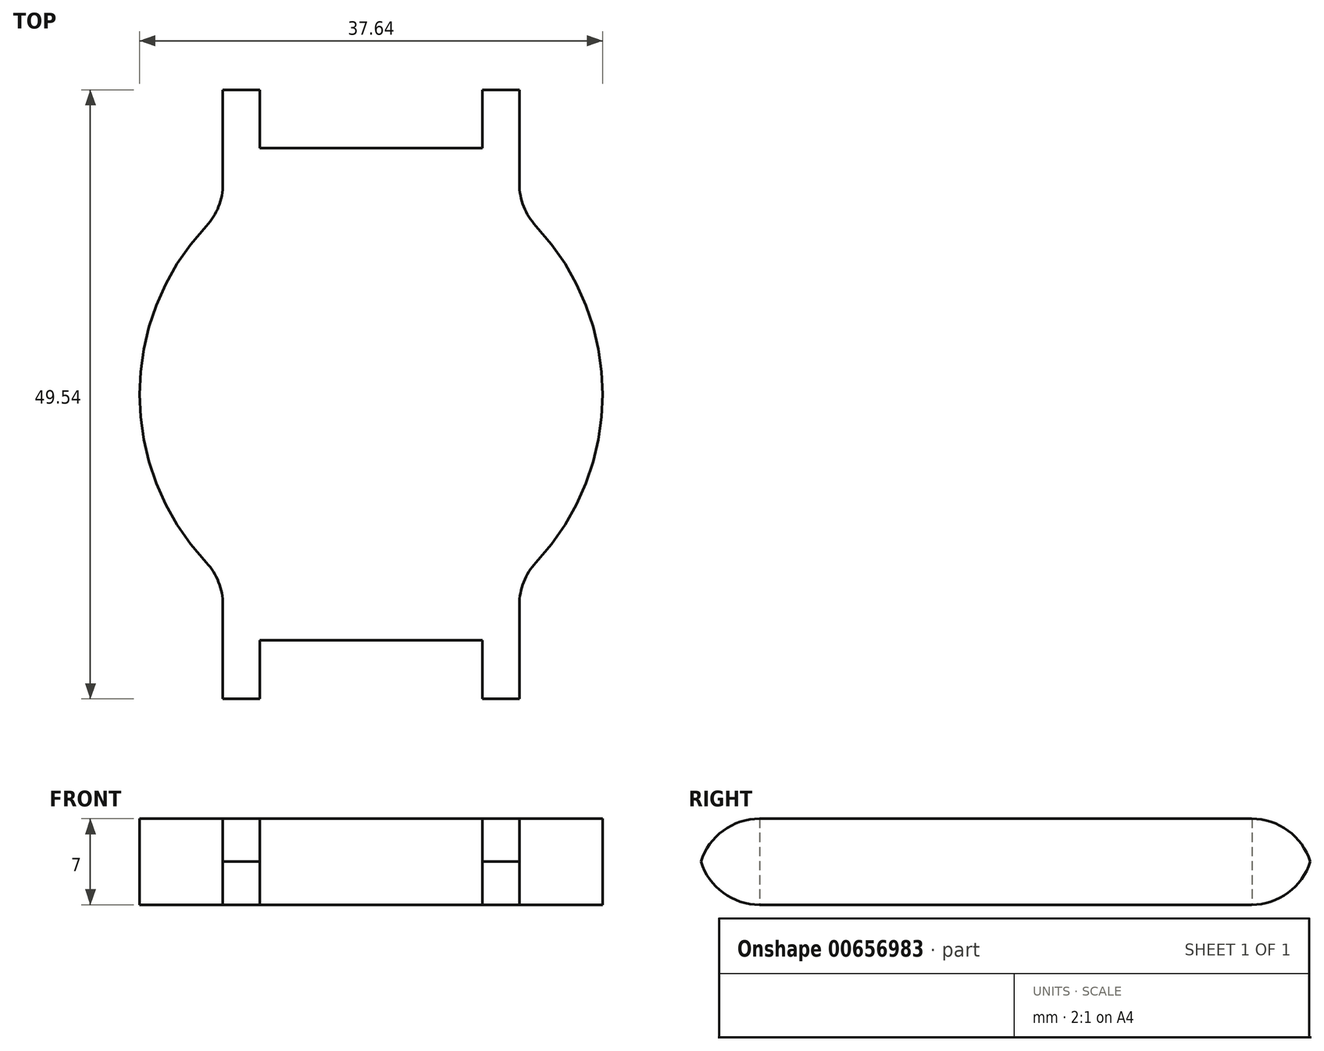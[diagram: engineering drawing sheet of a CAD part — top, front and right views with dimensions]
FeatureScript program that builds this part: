
annotation { "Feature Type Name" : "Feature", "Feature Type Description" : "" }
export const myFeature = defineFeature(function(context is Context, id is Id, definition is map)
    precondition{}
    {
        {
            var Q0;
            Q0=qCreatedBy(makeId("Top.planeOp"),FACE);
            var sketch = newSketch(context, id + "F0", { "sketchPlane" : qUnion([Q0])});
            skLineSegment(sketch, "E0", {"start": v(0, 25) * mm, "end": v(-12.05, 25) * mm});
            skLineSegment(sketch, "E1", {"start": v(0, 25) * mm, "end": v(12.05, 25) * mm});
            skLineSegment(sketch, "E2", {"start": v(-12.05, 25) * mm, "end": v(-12.05, 15) * mm});
            skLineSegment(sketch, "E3", {"start": v(12.05, 25) * mm, "end": v(12.05, 15) * mm});
            skLineSegment(sketch, "E4", {"start": v(0, -25) * mm, "end": v(-12.05, -25) * mm});
            skLineSegment(sketch, "E5", {"start": v(0, -25) * mm, "end": v(12.05, -25) * mm});
            skLineSegment(sketch, "E6", {"start": v(-12.05, -25) * mm, "end": v(-12.05, -15) * mm});
            skLineSegment(sketch, "E7", {"start": v(12.05, -25) * mm, "end": v(12.05, -15) * mm});
            skArc(sketch, "E8", {"start": v(12.05, -15) * mm, "mid": v(18.82, 0) * mm, "end": v(12.05, 15) * mm});
            skArc(sketch, "E9", {"start": v(-12.05, 15) * mm, "mid": v(-18.82, 0) * mm, "end": v(-12.05, -15) * mm});
            skSolve(sketch);
        }
        {
            var Q0;
            Q0=makeQuery(id+"F0.imprint","IMPRINT",FACE,{"disambiguationData":[TD([[makeQuery(id+"F0.imprint","IMPRINT",EDGE,{"derivedFrom":sQuery(id+"F0.wireOp",EDGE,"E0")}),1.0]])]});
            extrude(context, id + "F1", {"entities" : qUnion([Q0]), "depth" : 7 * mm, "offsetDistance" : 25 * mm});
        }
        {
            var Q0;
            Q0=qCreatedBy(makeId("Top.planeOp"),FACE);
            var sketch = newSketch(context, id + "F2", { "sketchPlane" : qUnion([Q0])});
            skLineSegment(sketch, "E10.bottom", {"start": v(-9.05, 20.03) * mm, "end": v(9.05, 20.03) * mm});
            skLineSegment(sketch, "E10.top", {"start": v(-9.05, 25.03) * mm, "end": v(9.05, 25.03) * mm});
            skLineSegment(sketch, "E10.left", {"start": v(-9.05, 25.03) * mm, "end": v(-9.05, 20.03) * mm});
            skLineSegment(sketch, "E10.right", {"start": v(9.05, 25.03) * mm, "end": v(9.05, 20.03) * mm});
            skLineSegment(sketch, "E11.bottom", {"start": v(-9.05, -20.01) * mm, "end": v(9.05, -20.01) * mm});
            skLineSegment(sketch, "E11.top", {"start": v(-9.05, -25.01) * mm, "end": v(9.05, -25.01) * mm});
            skLineSegment(sketch, "E11.left", {"start": v(-9.05, -25.01) * mm, "end": v(-9.05, -20.01) * mm});
            skLineSegment(sketch, "E11.right", {"start": v(9.05, -25.01) * mm, "end": v(9.05, -20.01) * mm});
            skSolve(sketch);
        }
        {
            var Q0;
            Q0=makeQuery(id+"F2.imprint","IMPRINT",FACE,{"disambiguationData":[TD([[makeQuery(id+"F2.imprint","IMPRINT",EDGE,{"derivedFrom":sQuery(id+"F2.wireOp",EDGE,"E10.bottom")}),1.0]])]});
            var Q1;
            Q1=makeQuery(id+"F2.imprint","IMPRINT",FACE,{"disambiguationData":[TD([[makeQuery(id+"F2.imprint","IMPRINT",EDGE,{"derivedFrom":sQuery(id+"F2.wireOp",EDGE,"E11.bottom")}),-1.0]])]});
            extrude(context, id + "F3", {"entities" : qUnion([Q0, Q1]), "operationType" : NewBodyOperationType.REMOVE, "depth" : 25 * mm, "offsetDistance" : 25 * mm});
        }
        {
            var Q0;
            {var subQ0=sQuery(id+"F0.wireOp",EDGE,"E6");var subQ1=sQuery(id+"F0.wireOp",EDGE,"E5");var subQ2=sQuery(id+"F0.wireOp",EDGE,"E4");Q0=makeQuery(id+"F3.boolean.opBoolean","SPLIT",EDGE,{"disambiguationData":[TD([makeQuery(id+"F1.opExtrude","SWEPT_FACE",FACE,{"disambiguationData":[OSD([subQ0])]})])],"derivedFrom":makeQuery(id+"F1.opExtrude","CAP_EDGE",EDGE,{"disambiguationData":[OSD([subQ2,subQ1])],"isStart":false})});}
            var Q1;
            {var subQ0=sQuery(id+"F0.wireOp",EDGE,"E6");var subQ1=sQuery(id+"F0.wireOp",EDGE,"E5");var subQ2=sQuery(id+"F0.wireOp",EDGE,"E4");Q1=makeQuery(id+"F3.boolean.opBoolean","SPLIT",EDGE,{"disambiguationData":[TD([makeQuery(id+"F1.opExtrude","SWEPT_FACE",FACE,{"disambiguationData":[OSD([subQ0])]})])],"derivedFrom":makeQuery(id+"F1.opExtrude","CAP_EDGE",EDGE,{"disambiguationData":[OSD([subQ2,subQ1])],"isStart":true})});}
            var Q2;
            {var subQ0=sQuery(id+"F0.wireOp",EDGE,"E1");var subQ1=sQuery(id+"F0.wireOp",EDGE,"E0");var subQ2=sQuery(id+"F0.wireOp",EDGE,"E2");Q2=makeQuery(id+"F3.boolean.opBoolean","SPLIT",EDGE,{"disambiguationData":[TD([makeQuery(id+"F1.opExtrude","SWEPT_FACE",FACE,{"disambiguationData":[OSD([subQ2])]})])],"derivedFrom":makeQuery(id+"F1.opExtrude","CAP_EDGE",EDGE,{"disambiguationData":[OSD([subQ1,subQ0])],"isStart":false})});}
            var Q3;
            {var subQ0=sQuery(id+"F0.wireOp",EDGE,"E1");var subQ1=sQuery(id+"F0.wireOp",EDGE,"E0");var subQ2=sQuery(id+"F0.wireOp",EDGE,"E2");Q3=makeQuery(id+"F3.boolean.opBoolean","SPLIT",EDGE,{"disambiguationData":[TD([makeQuery(id+"F1.opExtrude","SWEPT_FACE",FACE,{"disambiguationData":[OSD([subQ2])]})])],"derivedFrom":makeQuery(id+"F1.opExtrude","CAP_EDGE",EDGE,{"disambiguationData":[OSD([subQ1,subQ0])],"isStart":true})});}
            var Q4;
            Q4=makeQuery(id+"F1.opExtrude","SWEPT_EDGE",EDGE,{"disambiguationData":[OSD([sQuery(id+"F0.wireOp",EDGE,"E3"),sQuery(id+"F0.wireOp",EDGE,"E8")])]});
            var Q5;
            Q5=makeQuery(id+"F1.opExtrude","SWEPT_EDGE",EDGE,{"disambiguationData":[OSD([sQuery(id+"F0.wireOp",EDGE,"E7"),sQuery(id+"F0.wireOp",EDGE,"E8")])]});
            var Q6;
            Q6=makeQuery(id+"F1.opExtrude","SWEPT_EDGE",EDGE,{"disambiguationData":[OSD([sQuery(id+"F0.wireOp",EDGE,"E6"),sQuery(id+"F0.wireOp",EDGE,"E9")])]});
            var Q7;
            Q7=makeQuery(id+"F1.opExtrude","SWEPT_EDGE",EDGE,{"disambiguationData":[OSD([sQuery(id+"F0.wireOp",EDGE,"E2"),sQuery(id+"F0.wireOp",EDGE,"E9")])]});
            fillet(context, id + "F4", {"entities" : qUnion([Q0, Q1, Q2, Q3, Q4, Q5, Q6, Q7]), "radius" : 5 * mm, "tangentPropagation" : true, "allowEdgeOverflow" : false});
        }
    });
